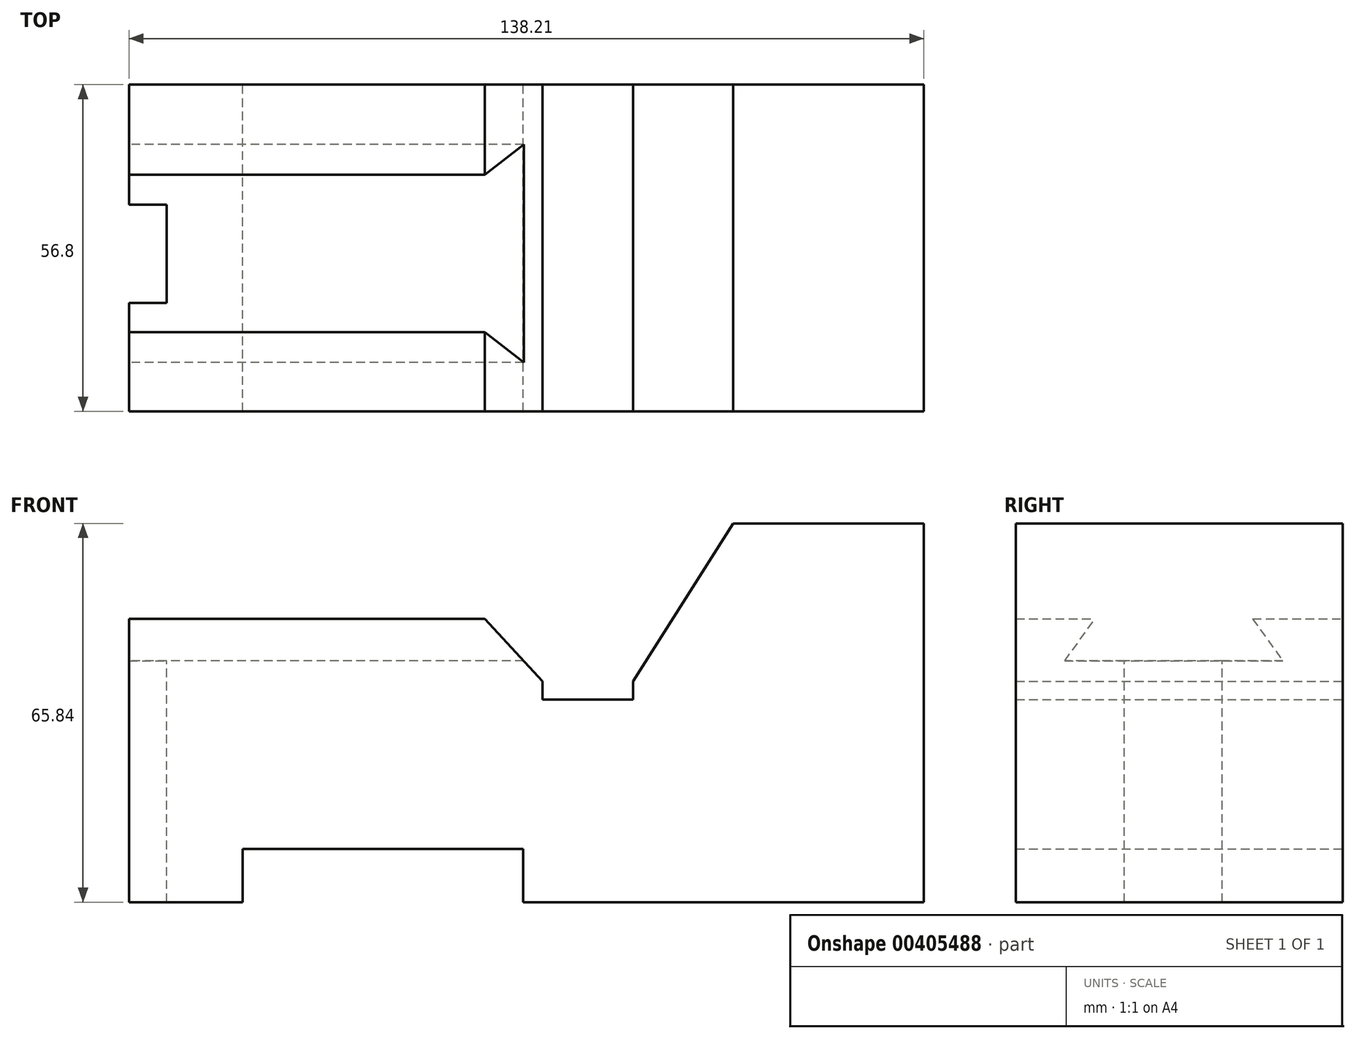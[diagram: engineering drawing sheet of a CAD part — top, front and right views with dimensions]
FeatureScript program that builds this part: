
annotation { "Feature Type Name" : "Feature", "Feature Type Description" : "" }
export const myFeature = defineFeature(function(context is Context, id is Id, definition is map)
    precondition{}
    {
        {
            var Q0;
            Q0=qCreatedBy(makeId("Front.planeOp"),FACE);
            var sketch = newSketch(context, id + "F0", { "sketchPlane" : qUnion([Q0])});
            skLineSegment(sketch, "E0.bottom", {"start": v(-42.72, 18.97) * mm, "end": v(19.13, 18.97) * mm});
            skLineSegment(sketch, "E0.top", {"start": v(-42.72, -30.29) * mm, "end": v(-22.96, -30.29) * mm});
            skLineSegment(sketch, "E0.left", {"start": v(-42.72, 18.97) * mm, "end": v(-42.72, -30.29) * mm});
            skLineSegment(sketch, "E1.bottom", {"start": v(54.52, -30.29) * mm, "end": v(95.49, -30.29) * mm});
            skLineSegment(sketch, "E1.top", {"start": v(62.3, 35.55) * mm, "end": v(95.49, 35.55) * mm});
            skLineSegment(sketch, "E1.right", {"start": v(95.49, -30.29) * mm, "end": v(95.49, 35.55) * mm});
            skLineSegment(sketch, "E2.top", {"start": v(-22.96, -21.04) * mm, "end": v(25.82, -21.04) * mm});
            skLineSegment(sketch, "E2.left", {"start": v(-22.96, -30.29) * mm, "end": v(-22.96, -21.04) * mm});
            skLineSegment(sketch, "E2.right", {"start": v(25.82, -30.29) * mm, "end": v(25.82, -21.04) * mm});
            skLineSegment(sketch, "E3", {"start": v(19.13, 18.97) * mm, "end": v(29.17, 8.13) * mm});
            skLineSegment(sketch, "E4", {"start": v(29.17, 8.13) * mm, "end": v(29.17, 4.94) * mm});
            skLineSegment(sketch, "E5", {"start": v(29.17, 4.94) * mm, "end": v(44.95, 4.94) * mm});
            skLineSegment(sketch, "E6", {"start": v(44.95, 4.94) * mm, "end": v(44.95, 8.13) * mm});
            skLineSegment(sketch, "E7", {"start": v(44.95, 8.13) * mm, "end": v(62.3, 35.55) * mm});
            skLineSegment(sketch, "E8.trimOffspring", {"start": v(25.82, -30.29) * mm, "end": v(54.52, -30.29) * mm});
            skSolve(sketch);
        }
        {
            var Q0;
            Q0 = qSketchRegion(id + "F0", true);
            extrude(context, id + "F1", {"entities" : qUnion([Q0]), "endBound" : BoundingType.SYMMETRIC, "depth" : 56.8 * mm});
        }
        {
            var Q0;
            Q0=makeQuery(id+"F1.opExtrude","SWEPT_FACE",FACE,{"disambiguationData":[OSD([sQuery(id+"F0.wireOp",EDGE,"E0.left")])]});
            var sketch = newSketch(context, id + "F2", { "sketchPlane" : qUnion([Q0])});
            skLineSegment(sketch, "E9", {"start": v(-12.75, 18.97) * mm, "end": v(-18.01, 11.64) * mm});
            skLineSegment(sketch, "E10", {"start": v(-18.01, 11.64) * mm, "end": v(19.93, 11.64) * mm});
            skLineSegment(sketch, "E11", {"start": v(19.93, 11.64) * mm, "end": v(14.67, 18.97) * mm});
            skSolve(sketch);
        }
        {
            var Q0;
            {var subQ0=sQuery(id+"F2.wireOp",EDGE,"E9");Q0=makeQuery(id+"F2.imprint","IMPRINT",FACE,{"disambiguationData":[TD([[makeQuery(id+"F2.imprint","IMPRINT",EDGE,{"derivedFrom":subQ0}),1.0]])]});}
            extrude(context, id + "F3", {"entities" : qUnion([Q0]), "operationType" : NewBodyOperationType.REMOVE, "oppositeDirection" : true, "depth" : 71.3 * mm});
        }
        {
            var Q0;
            Q0=makeQuery(id+"F3.boolean.opBoolean","COPY",FACE,{"derivedFrom":makeQuery(id+"F3.opExtrude","SWEPT_FACE",FACE,{"disambiguationData":[OSD([sQuery(id+"F2.wireOp",EDGE,"E10")])]})});
            var sketch = newSketch(context, id + "F4", { "sketchPlane" : qUnion([Q0])});
            skLineSegment(sketch, "E12.bottom", {"start": v(-42.72, 7.5) * mm, "end": v(-36.14, 7.5) * mm});
            skLineSegment(sketch, "E12.top", {"start": v(-42.72, -9.56) * mm, "end": v(-36.14, -9.56) * mm});
            skLineSegment(sketch, "E12.left", {"start": v(-42.72, 7.5) * mm, "end": v(-42.72, -9.56) * mm});
            skLineSegment(sketch, "E12.right", {"start": v(-36.14, 7.5) * mm, "end": v(-36.14, -9.56) * mm});
            skSolve(sketch);
        }
        {
            var Q0;
            Q0 = qSketchRegion(id + "F4", true);
            extrude(context, id + "F5", {"entities" : qUnion([Q0]), "operationType" : NewBodyOperationType.REMOVE, "oppositeDirection" : true, "depth" : 70.5 * mm});
        }
    });
